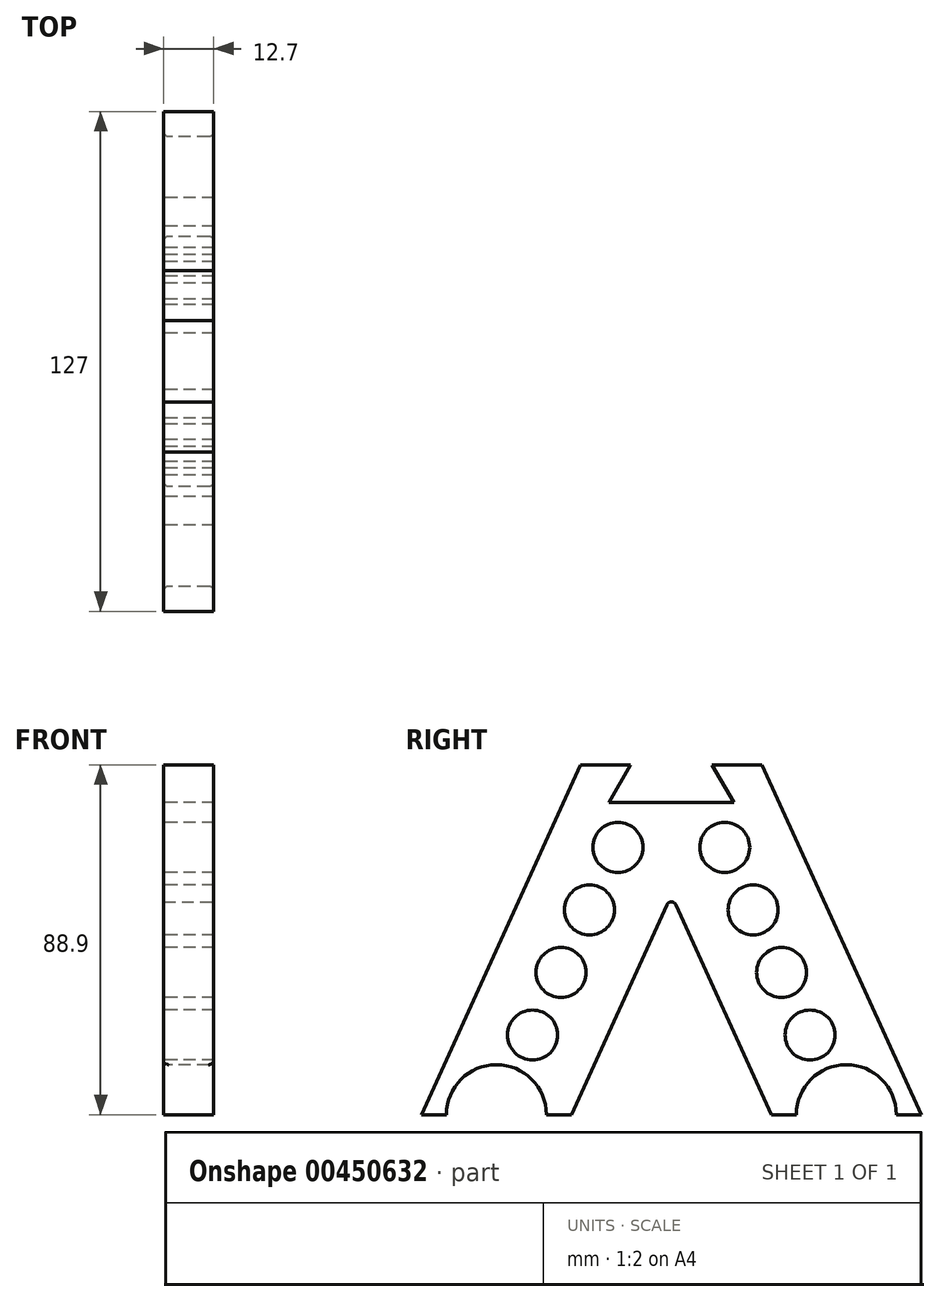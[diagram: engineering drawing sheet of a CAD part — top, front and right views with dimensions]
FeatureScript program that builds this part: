
annotation { "Feature Type Name" : "Feature", "Feature Type Description" : "" }
export const myFeature = defineFeature(function(context is Context, id is Id, definition is map)
    precondition{}
    {
        {
            var Q0;
            Q0=qCreatedBy(makeId("Right.planeOp"),FACE);
            var sketch = newSketch(context, id + "F0", { "sketchPlane" : qUnion([Q0])});
            skLineSegment(sketch, "E0", {"start": v(-63.5, 0) * mm, "end": v(-57.15, 0) * mm});
            skArc(sketch, "E1", {"start": v(-57.15, 0) * mm, "mid": v(-44.45, 12.7) * mm, "end": v(-31.75, 0) * mm});
            skLineSegment(sketch, "E2", {"start": v(-63.5, 0) * mm, "end": v(-23.08, 88.9) * mm});
            skLineSegment(sketch, "E3", {"start": v(-23.08, 88.9) * mm, "end": v(-10.38, 88.9) * mm});
            skLineSegment(sketch, "E4", {"start": v(-10.38, 88.9) * mm, "end": v(-15.88, 79.38) * mm});
            skLineSegment(sketch, "E5", {"start": v(-15.88, 79.38) * mm, "end": v(0, 79.38) * mm});
            skLineSegment(sketch, "E6", {"start": v(-31.75, 0) * mm, "end": v(-25.4, 0) * mm});
            skLineSegment(sketch, "E7", {"start": v(-25.4, 0) * mm, "end": v(0, 55.86) * mm});
            skLineSegment(sketch, "E8", {"start": v(0, 55.86) * mm, "end": v(0, 79.38) * mm});
            skCircle(sketch, "E9", {"center": v(-13.57, 67.92) * mm, "radius": 6.35 * mm});
            skCircle(sketch, "E10", {"center": v(-20.8, 52.02) * mm, "radius": 6.35 * mm});
            skCircle(sketch, "E11", {"center": v(-28.02, 36.13) * mm, "radius": 6.35 * mm});
            skCircle(sketch, "E12", {"center": v(-35.25, 20.23) * mm, "radius": 6.35 * mm});
            skLineSegment(sketch, "E13", {"start": v(-44.45, 0) * mm, "end": v(-35.25, 20.23) * mm, "construction": true});
            skLineSegment(sketch, "E14", {"start": v(-35.25, 20.23) * mm, "end": v(-28.02, 36.13) * mm, "construction": true});
            skLineSegment(sketch, "E15", {"start": v(-28.02, 36.13) * mm, "end": v(-20.8, 52.02) * mm, "construction": true});
            skLineSegment(sketch, "E16", {"start": v(-20.8, 52.02) * mm, "end": v(-13.57, 67.92) * mm, "construction": true});
            skSolve(sketch);
        }
        {
            var Q0;
            Q0 = qSketchRegion(id + "F0", true);
            extrude(context, id + "F1", {"entities" : qUnion([Q0]), "depth" : 12.7 * mm});
        }
        {
            var Q0;
            Q0=makeQuery(id+"F1.opExtrude","SWEPT_BODY",BODY,{"disambiguationData":[OSD([sQuery(id+"F0.wireOp",EDGE,"E0"),sQuery(id+"F0.wireOp",EDGE,"E1"),sQuery(id+"F0.wireOp",EDGE,"E2"),sQuery(id+"F0.wireOp",EDGE,"E3"),sQuery(id+"F0.wireOp",EDGE,"E4"),sQuery(id+"F0.wireOp",EDGE,"E5"),sQuery(id+"F0.wireOp",EDGE,"E6"),sQuery(id+"F0.wireOp",EDGE,"E7"),sQuery(id+"F0.wireOp",EDGE,"E8")])]});
            var Q1;
            Q1=qCreatedBy(makeId("Front.planeOp"),FACE);
            mirror(context, id + "F2", {"operationType" : NewBodyOperationType.ADD, "entities" : qUnion([Q0]), "mirrorPlane" : qUnion([Q1])});
        }
        {
            var Q0;
            Q0=makeQuery(id+"F2.opPattern","COPY",EDGE,{"derivedFrom":makeQuery(id+"F1.opExtrude","CAP_EDGE",EDGE,{"disambiguationData":[OSD([sQuery(id+"F0.wireOp",EDGE,"E1")])],"isStart":false}),"instanceName":"1"});
            var Q1;
            Q1=makeQuery(id+"F2.opPattern","COPY",EDGE,{"derivedFrom":makeQuery(id+"F1.opExtrude","CAP_EDGE",EDGE,{"disambiguationData":[OSD([sQuery(id+"F0.wireOp",EDGE,"E1")])],"isStart":true}),"instanceName":"1"});
            var Q2;
            Q2=makeQuery(id+"F1.opExtrude","CAP_EDGE",EDGE,{"disambiguationData":[OSD([sQuery(id+"F0.wireOp",EDGE,"E1")])],"isStart":true});
            var Q3;
            Q3=makeQuery(id+"F1.opExtrude","CAP_EDGE",EDGE,{"disambiguationData":[OSD([sQuery(id+"F0.wireOp",EDGE,"E1")])],"isStart":false});
            var Q4;
            {var subQ0=makeQuery(id+"F1.opExtrude","SWEPT_EDGE",EDGE,{"disambiguationData":[OSD([sQuery(id+"F0.wireOp",EDGE,"E7"),sQuery(id+"F0.wireOp",EDGE,"E8")])]});Q4=makeQuery(id+"F2.boolean.opBoolean","MERGE",EDGE,{"derivedFrom":[subQ0,makeQuery(id+"F2.opPattern","COPY",EDGE,{"derivedFrom":subQ0,"instanceName":"1"})]});}
            fillet(context, id + "F3", {"entities" : qUnion([Q0, Q1, Q2, Q3, Q4]), "radius" : 1.27 * mm, "tangentPropagation" : true, "allowEdgeOverflow" : false});
        }
    });
